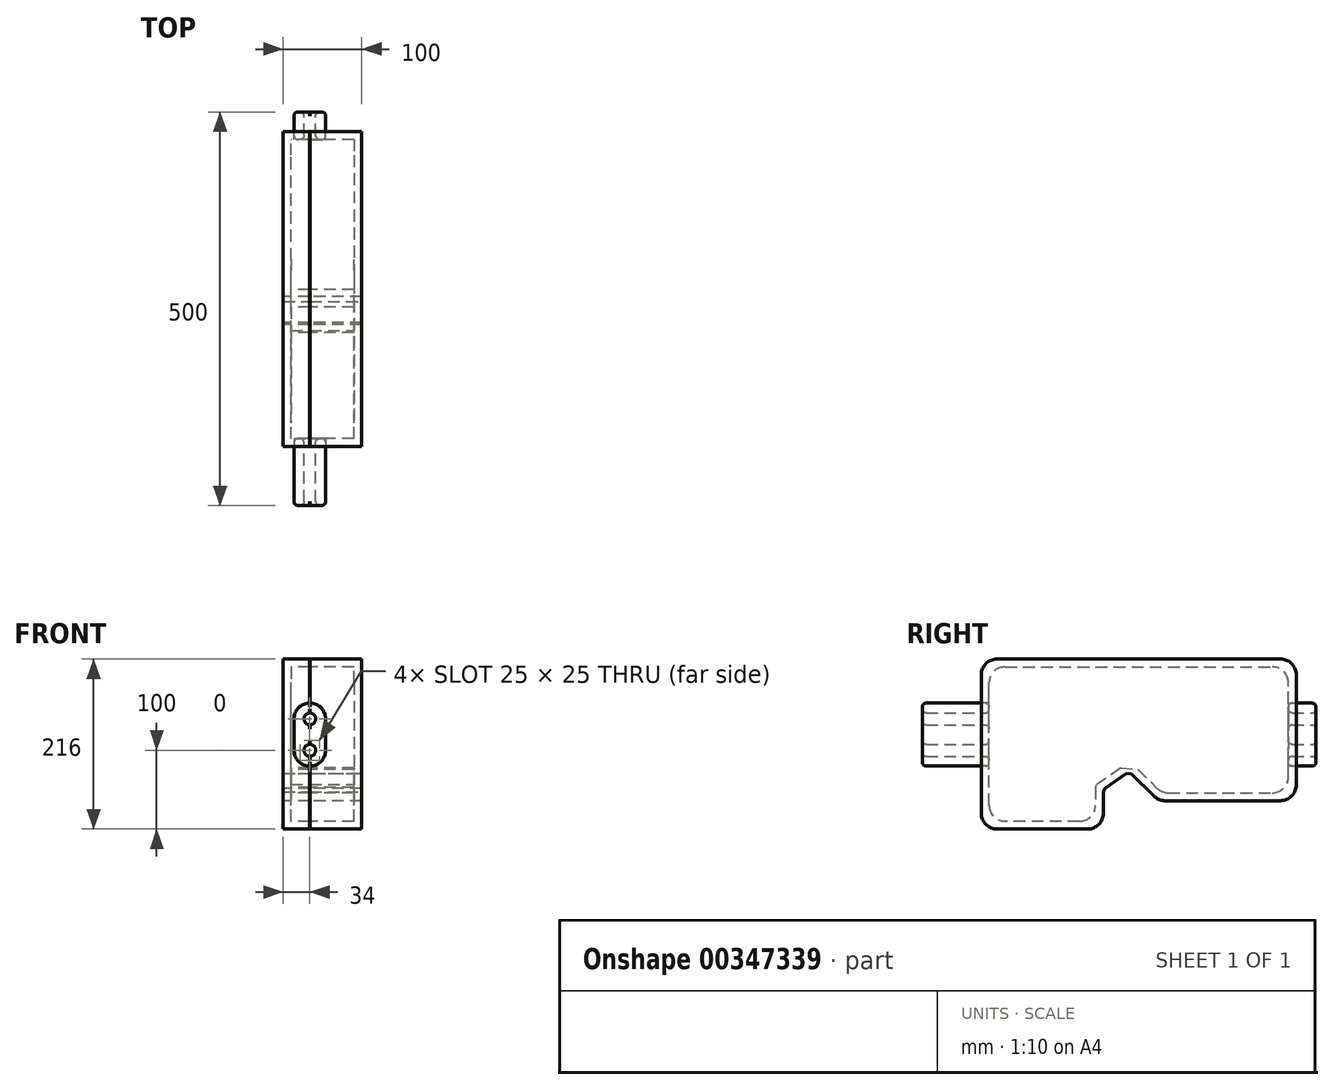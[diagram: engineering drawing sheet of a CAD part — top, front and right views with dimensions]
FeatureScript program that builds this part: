
annotation { "Feature Type Name" : "Feature", "Feature Type Description" : "" }
export const myFeature = defineFeature(function(context is Context, id is Id, definition is map)
    precondition{}
    {
        {
            var Q0;
            Q0=qCreatedBy(makeId("Right.planeOp"),FACE);
            var sketch = newSketch(context, id + "F0", { "sketchPlane" : qUnion([Q0])});
            skLineSegment(sketch, "E0.bottom", {"start": v(200, 75) * mm, "end": v(-200, 75) * mm});
            skLineSegment(sketch, "E0.left", {"start": v(200, 75) * mm, "end": v(200, -75) * mm});
            skLineSegment(sketch, "E0.right", {"start": v(-200, 75) * mm, "end": v(-200, -75) * mm});
            skPoint(sketch, "E0.middle", {"position": v(0, 0) * mm});
            skLineSegment(sketch, "E1", {"start": v(-200, -75) * mm, "end": v(-200, -141) * mm});
            skLineSegment(sketch, "E2", {"start": v(-200, -141) * mm, "end": v(-45, -141) * mm});
            skLineSegment(sketch, "E3", {"start": v(-45, -141) * mm, "end": v(-45, -91) * mm});
            skLineSegment(sketch, "E4", {"start": v(-12.23, -68.06) * mm, "end": v(-87.83, -68.06) * mm, "construction": true});
            skLineSegment(sketch, "E5", {"start": v(200, -75) * mm, "end": v(200, -105) * mm});
            skLineSegment(sketch, "E6", {"start": v(200, -105) * mm, "end": v(25, -105) * mm});
            skLineSegment(sketch, "E7", {"start": v(25, -105) * mm, "end": v(-12.23, -68.06) * mm});
            skLineSegment(sketch, "E8", {"start": v(-45, -91) * mm, "end": v(-12.23, -68.06) * mm});
            skSolve(sketch);
        }
        {
            var Q0;
            Q0=makeQuery(id+"F0.imprint","IMPRINT",FACE,{"disambiguationData":[TD([[makeQuery(id+"F0.imprint","IMPRINT",EDGE,{"derivedFrom":sQuery(id+"F0.wireOp",EDGE,"E0.bottom")}),1.0]])]});
            extrude(context, id + "F1", {"entities" : qUnion([Q0]), "depth" : 100 * mm});
        }
        {
            var Q0;
            Q0=makeQuery(id+"F1.opExtrude","CAP_FACE",FACE,{"disambiguationData":[OSD([sQuery(id+"F0.wireOp",EDGE,"E0.bottom"),sQuery(id+"F0.wireOp",EDGE,"E0.top"),sQuery(id+"F0.wireOp",EDGE,"E0.left"),sQuery(id+"F0.wireOp",EDGE,"E0.right")])],"isStart":true});
            shell(context, id + "F2", {"entities" : qUnion([Q0]), "thickness" : 10 * mm});
        }
        {
            var Q0;
            Q0=makeQuery(id+"F1.opExtrude","SWEPT_FACE",FACE,{"disambiguationData":[OSD([sQuery(id+"F0.wireOp",EDGE,"E0.left")])]});
            var sketch = newSketch(context, id + "F3", { "sketchPlane" : qUnion([Q0])});
            skCircle(sketch, "E9", {"center": v(-34, -41) * mm, "radius": 7.5 * mm});
            skCircle(sketch, "E10", {"center": v(-34, -1) * mm, "radius": 7.5 * mm});
            skLineSegment(sketch, "E11", {"start": v(-34, -1) * mm, "end": v(-34, -41) * mm, "construction": true});
            skLineSegment(sketch, "E12", {"start": v(-34, -1) * mm, "end": v(-100, -1) * mm, "construction": true});
            skLineSegment(sketch, "E13", {"start": v(-34, -1) * mm, "end": v(0, -1) * mm, "construction": true});
            skSolve(sketch);
        }
        {
            var Q0;
            Q0=qSketchRegion(id+"F3",true);
            extrude(context, id + "F4", {"entities" : qUnion([Q0]), "operationType" : NewBodyOperationType.REMOVE, "oppositeDirection" : true, "depth" : 1000 * mm});
        }
        {
            var Q0;
            Q0=makeQuery(id+"F1.opExtrude","CAP_FACE",FACE,{"disambiguationData":[OSD([sQuery(id+"F0.wireOp",EDGE,"E0.bottom"),sQuery(id+"F0.wireOp",EDGE,"E0.top"),sQuery(id+"F0.wireOp",EDGE,"E0.left"),sQuery(id+"F0.wireOp",EDGE,"E0.right")])],"isStart":true});
            var sketch = newSketch(context, id + "F5", { "sketchPlane" : qUnion([Q0])});
            skLineSegment(sketch, "E14", {"start": v(200, -141) * mm, "end": v(200, 75) * mm});
            skLineSegment(sketch, "E15", {"start": v(200, 75) * mm, "end": v(-200, 75) * mm});
            skLineSegment(sketch, "E16", {"start": v(-200, 75) * mm, "end": v(-200, 75) * mm});
            skLineSegment(sketch, "E17", {"start": v(45, -141) * mm, "end": v(45, -141) * mm});
            skLineSegment(sketch, "E18", {"start": v(45, -141) * mm, "end": v(200, -141) * mm});
            skLineSegment(sketch, "E19", {"start": v(-200, 75) * mm, "end": v(-200, -105) * mm});
            skLineSegment(sketch, "E20", {"start": v(-200, -105) * mm, "end": v(-200, -105) * mm});
            skLineSegment(sketch, "E21", {"start": v(-200, -105) * mm, "end": v(-25, -105) * mm});
            skLineSegment(sketch, "E22", {"start": v(-25, -105) * mm, "end": v(12.23, -68.06) * mm});
            skLineSegment(sketch, "E23", {"start": v(12.23, -68.06) * mm, "end": v(45, -91) * mm});
            skLineSegment(sketch, "E24", {"start": v(45, -91) * mm, "end": v(45, -141) * mm});
            skSolve(sketch);
        }
        {
            var Q0;
            Q0=qSketchRegion(id+"F5",true);
            extrude(context, id + "F6", {"entities" : qUnion([Q0]), "operationType" : NewBodyOperationType.ADD, "oppositeDirection" : true, "depth" : 10 * mm});
        }
        {
            var Q0;
            Q0=makeQuery(id+"F1.opExtrude","SWEPT_FACE",FACE,{"disambiguationData":[OSD([sQuery(id+"F0.wireOp",EDGE,"E2")])]});
            var sketch = newSketch(context, id + "F7", { "sketchPlane" : qUnion([Q0])});
            skLineSegment(sketch, "E25.bottom", {"start": v(33.95, 216.16) * mm, "end": v(34.05, 216.16) * mm});
            skLineSegment(sketch, "E25.top", {"start": v(33.95, -216.16) * mm, "end": v(34.05, -216.16) * mm});
            skLineSegment(sketch, "E25.left", {"start": v(33.95, 216.16) * mm, "end": v(33.95, -216.16) * mm});
            skLineSegment(sketch, "E25.right", {"start": v(34.05, 216.16) * mm, "end": v(34.05, -216.16) * mm});
            skPoint(sketch, "E25.middle", {"position": v(34, 0) * mm});
            skSolve(sketch);
        }
        {
            var Q0;
            Q0=qSketchRegion(id+"F7",true);
            extrude(context, id + "F8", {"entities" : qUnion([Q0]), "operationType" : NewBodyOperationType.REMOVE, "oppositeDirection" : true, "depth" : 583 * mm});
        }
        {
            var Q0;
            {var subQ0=sQuery(id+"F0.wireOp",EDGE,"E5");var subQ1=sQuery(id+"F0.wireOp",EDGE,"E0.left");var subQ2=makeQuery(id+"F1.opExtrude","SWEPT_FACE",FACE,{"disambiguationData":[OSD([subQ1,subQ0])]});Q0=makeQuery(id+"F8.boolean.opBoolean","SPLIT",FACE,{"disambiguationData":[TD([makeQuery(id+"F8.opExtrude","SWEPT_FACE",FACE,{"disambiguationData":[OSD([sQuery(id+"F7.wireOp",EDGE,"E25.right")])]})])],"derivedFrom":subQ2});}
            var sketch = newSketch(context, id + "F9", { "sketchPlane" : qUnion([Q0])});
            skLineSegment(sketch, "E26", {"start": v(-34, -1) * mm, "end": v(-34, -41) * mm, "construction": true});
            skLineSegment(sketch, "E27", {"start": v(-34, -1) * mm, "end": v(-14, -1) * mm, "construction": true});
            skLineSegment(sketch, "E28", {"start": v(-34, -1) * mm, "end": v(-54, -1) * mm, "construction": true});
            skArc(sketch, "E29", {"start": v(-14, -1) * mm, "mid": v(-34, 19) * mm, "end": v(-54, -1) * mm});
            skArc(sketch, "E30", {"start": v(-54, -41) * mm, "mid": v(-34, -61) * mm, "end": v(-14, -41) * mm});
            skPoint(sketch, "E30.endSnap0", {"position": v(-26.5, -41) * mm});
            skLineSegment(sketch, "E31", {"start": v(-14, -1) * mm, "end": v(-14, -41) * mm});
            skLineSegment(sketch, "E32", {"start": v(-54, -1) * mm, "end": v(-54, -41) * mm});
            skArc(sketch, "E33.0", {"start": v(-13.9, -1) * mm, "mid": v(-34, 19.1) * mm, "end": v(-54.1, -1) * mm});
            skLineSegment(sketch, "E33.1", {"start": v(-13.9, -1) * mm, "end": v(-13.9, -41) * mm});
            skArc(sketch, "E33.2", {"start": v(-54.1, -41) * mm, "mid": v(-34, -61.1) * mm, "end": v(-13.9, -41) * mm});
            skLineSegment(sketch, "E33.3", {"start": v(-54.1, -1) * mm, "end": v(-54.1, -41) * mm});
            skSolve(sketch);
        }
        {
            var Q0;
            Q0 = qSketchRegion(id + "F9", true);
            extrude(context, id + "F10", {"entities" : qUnion([Q0]), "operationType" : NewBodyOperationType.REMOVE, "oppositeDirection" : true, "depth" : 25 * mm});
        }
        {
            var Q0;
            {var subQ1=sQuery(id+"F0.wireOp",EDGE,"E1");var subQ2=sQuery(id+"F0.wireOp",EDGE,"E0.right");var subQ4=makeQuery(id+"F1.opExtrude","SWEPT_FACE",FACE,{"disambiguationData":[OSD([subQ2,subQ1])]});Q0=makeQuery(id+"F8.boolean.opBoolean","SPLIT",FACE,{"disambiguationData":[TD([makeQuery(id+"F8.opExtrude","SWEPT_FACE",FACE,{"disambiguationData":[OSD([sQuery(id+"F7.wireOp",EDGE,"E25.right")])]})])],"derivedFrom":subQ4});}
            var sketch = newSketch(context, id + "F11", { "sketchPlane" : qUnion([Q0])});
            skLineSegment(sketch, "E34", {"start": v(34, -41) * mm, "end": v(34, -1) * mm, "construction": true});
            skLineSegment(sketch, "E35", {"start": v(34, -1) * mm, "end": v(34, -41) * mm, "construction": true});
            skLineSegment(sketch, "E36", {"start": v(34, -1) * mm, "end": v(54, -1) * mm, "construction": true});
            skLineSegment(sketch, "E37", {"start": v(34, -1) * mm, "end": v(14, -1) * mm, "construction": true});
            skArc(sketch, "E38", {"start": v(54, -1) * mm, "mid": v(34, 19) * mm, "end": v(14, -1) * mm});
            skArc(sketch, "E39", {"start": v(14, -41) * mm, "mid": v(34, -61) * mm, "end": v(54, -41) * mm});
            skPoint(sketch, "E39.endSnap0", {"position": v(41.5, -41) * mm});
            skLineSegment(sketch, "E40", {"start": v(54, -1) * mm, "end": v(54, -41) * mm});
            skLineSegment(sketch, "E41", {"start": v(14, -1) * mm, "end": v(14, -41) * mm});
            skArc(sketch, "E42.0", {"start": v(54.1, -1) * mm, "mid": v(34, 19.1) * mm, "end": v(13.9, -1) * mm});
            skLineSegment(sketch, "E42.1", {"start": v(54.1, -1) * mm, "end": v(54.1, -41) * mm});
            skArc(sketch, "E42.2", {"start": v(13.9, -41) * mm, "mid": v(34, -61.1) * mm, "end": v(54.1, -41) * mm});
            skLineSegment(sketch, "E42.3", {"start": v(13.9, -1) * mm, "end": v(13.9, -41) * mm});
            skSolve(sketch);
        }
        {
            var Q0;
            Q0 = qSketchRegion(id + "F11", true);
            extrude(context, id + "F12", {"entities" : qUnion([Q0]), "operationType" : NewBodyOperationType.REMOVE, "oppositeDirection" : true, "depth" : 25 * mm});
        }
        {
            var Q0;
            {var subQ0=sQuery(id+"F0.wireOp",EDGE,"E5");var subQ1=sQuery(id+"F0.wireOp",EDGE,"E0.left");var subQ2=makeQuery(id+"F1.opExtrude","SWEPT_FACE",FACE,{"disambiguationData":[OSD([subQ1,subQ0])]});var subQ3=makeQuery(id+"F2.opShell","OFFSET_FACE",FACE,{"disambiguationData":[OSD([subQ1,subQ0])]});var subQ4=makeQuery(id+"F4.opExtrude","SWEPT_FACE",FACE,{"disambiguationData":[OSD([sQuery(id+"F3.wireOp",EDGE,"E10")])]});var subQ5=makeQuery(id+"F4.boolean.opBoolean","COPY",FACE,{"disambiguationData":[TD([subQ2])],"derivedFrom":subQ4});var subQ6=sQuery(id+"F0.wireOp",EDGE,"E0.bottom");var subQ7=sQuery(id+"F0.wireOp",EDGE,"E1");var subQ8=sQuery(id+"F0.wireOp",EDGE,"E0.right");var subQ9=makeQuery(id+"F1.opExtrude","SWEPT_FACE",FACE,{"disambiguationData":[OSD([subQ8,subQ7])]});var subQ10=makeQuery(id+"F2.opShell","OFFSET_FACE",FACE,{"disambiguationData":[OSD([subQ8,subQ7])]});Q0=makeQuery(id+"F10.boolean.opBoolean","SPLIT",FACE,{"disambiguationData":[TD([makeQuery(id+"F10.opExtrude","SWEPT_FACE",FACE,{"disambiguationData":[OSD([sQuery(id+"F9.wireOp",EDGE,"E29")])]})])],"derivedFrom":makeQuery(id+"F8.boolean.opBoolean","COPY",FACE,{"disambiguationData":[TD([makeQuery(id+"F1.opExtrude","SWEPT_FACE",FACE,{"disambiguationData":[OSD([subQ6])]}),subQ2,subQ9,makeQuery(id+"F2.opShell","OFFSET_FACE",FACE,{"disambiguationData":[OSD([subQ6])]}),subQ3,subQ10,subQ5,makeQuery(id+"F4.boolean.opBoolean","COPY",FACE,{"disambiguationData":[TD([subQ9])],"derivedFrom":subQ4})])],"derivedFrom":makeQuery(id+"F8.opExtrude","SWEPT_FACE",FACE,{"disambiguationData":[OSD([sQuery(id+"F7.wireOp",EDGE,"E25.right")])]})})});}
            var Q1;
            {var subQ0=sQuery(id+"F0.wireOp",EDGE,"E5");var subQ1=sQuery(id+"F0.wireOp",EDGE,"E0.left");var subQ2=makeQuery(id+"F1.opExtrude","SWEPT_FACE",FACE,{"disambiguationData":[OSD([subQ1,subQ0])]});var subQ3=makeQuery(id+"F2.opShell","OFFSET_FACE",FACE,{"disambiguationData":[OSD([subQ1,subQ0])]});Q1=makeQuery(id+"F8.boolean.opBoolean","COPY",FACE,{"disambiguationData":[TD([subQ2,subQ3,makeQuery(id+"F4.boolean.opBoolean","COPY",FACE,{"disambiguationData":[TD([subQ2])],"derivedFrom":makeQuery(id+"F4.opExtrude","SWEPT_FACE",FACE,{"disambiguationData":[OSD([sQuery(id+"F3.wireOp",EDGE,"E9")])]})}),makeQuery(id+"F4.boolean.opBoolean","COPY",FACE,{"disambiguationData":[TD([subQ2])],"derivedFrom":makeQuery(id+"F4.opExtrude","SWEPT_FACE",FACE,{"disambiguationData":[OSD([sQuery(id+"F3.wireOp",EDGE,"E10")])]})})])],"derivedFrom":makeQuery(id+"F8.opExtrude","SWEPT_FACE",FACE,{"disambiguationData":[OSD([sQuery(id+"F7.wireOp",EDGE,"E25.right")])]})});}
            var Q2;
            {var subQ0=sQuery(id+"F0.wireOp",EDGE,"E5");var subQ1=sQuery(id+"F0.wireOp",EDGE,"E0.left");var subQ2=makeQuery(id+"F1.opExtrude","SWEPT_FACE",FACE,{"disambiguationData":[OSD([subQ1,subQ0])]});var subQ3=makeQuery(id+"F2.opShell","OFFSET_FACE",FACE,{"disambiguationData":[OSD([subQ1,subQ0])]});var subQ4=makeQuery(id+"F4.opExtrude","SWEPT_FACE",FACE,{"disambiguationData":[OSD([sQuery(id+"F3.wireOp",EDGE,"E9")])]});var subQ5=makeQuery(id+"F4.boolean.opBoolean","COPY",FACE,{"disambiguationData":[TD([subQ2])],"derivedFrom":subQ4});var subQ6=sQuery(id+"F0.wireOp",EDGE,"548lelhJ-FumK-1v7O-jp4s-T3LJ27CFtbea");var subQ7=sQuery(id+"F0.wireOp",EDGE,"E2");var subQ8=sQuery(id+"F0.wireOp",EDGE,"BKIsQGDg-fWEg-7aJj-qOrJ-T1CRB7Qqrcyv");var subQ9=sQuery(id+"F0.wireOp",EDGE,"E1");var subQ10=sQuery(id+"F0.wireOp",EDGE,"E0.right");var subQ11=makeQuery(id+"F2.opShell","OFFSET_FACE",FACE,{"disambiguationData":[OSD([subQ10,subQ9])]});var subQ12=sQuery(id+"F0.wireOp",EDGE,"E6");var subQ13=makeQuery(id+"F1.opExtrude","SWEPT_FACE",FACE,{"disambiguationData":[OSD([subQ10,subQ9])]});var subQ14=sQuery(id+"F0.wireOp",EDGE,"E3");Q2=makeQuery(id+"F10.boolean.opBoolean","SPLIT",FACE,{"disambiguationData":[TD([makeQuery(id+"F10.opExtrude","SWEPT_FACE",FACE,{"disambiguationData":[OSD([sQuery(id+"F9.wireOp",EDGE,"E30")])]})])],"derivedFrom":makeQuery(id+"F8.boolean.opBoolean","COPY",FACE,{"disambiguationData":[TD([subQ2,subQ13,makeQuery(id+"F1.opExtrude","SWEPT_FACE",FACE,{"disambiguationData":[OSD([subQ7])]}),makeQuery(id+"F1.opExtrude","SWEPT_FACE",FACE,{"disambiguationData":[OSD([subQ14])]}),makeQuery(id+"F1.opExtrude","SWEPT_FACE",FACE,{"disambiguationData":[OSD([subQ12])]}),makeQuery(id+"F1.opExtrude","SWEPT_FACE",FACE,{"disambiguationData":[OSD([subQ8])]}),makeQuery(id+"F1.opExtrude","SWEPT_FACE",FACE,{"disambiguationData":[OSD([subQ6])]}),subQ3,subQ11,makeQuery(id+"F2.opShell","OFFSET_FACE",FACE,{"disambiguationData":[OSD([subQ7])]}),makeQuery(id+"F2.opShell","OFFSET_FACE",FACE,{"disambiguationData":[OSD([subQ14])]}),makeQuery(id+"F2.opShell","OFFSET_FACE",FACE,{"disambiguationData":[OSD([subQ12])]}),makeQuery(id+"F2.opShell","OFFSET_FACE",FACE,{"disambiguationData":[OSD([subQ8])]}),makeQuery(id+"F2.opShell","OFFSET_FACE",FACE,{"disambiguationData":[OSD([subQ6])]}),subQ5,makeQuery(id+"F4.boolean.opBoolean","COPY",FACE,{"disambiguationData":[TD([subQ13])],"derivedFrom":subQ4})])],"derivedFrom":makeQuery(id+"F8.opExtrude","SWEPT_FACE",FACE,{"disambiguationData":[OSD([sQuery(id+"F7.wireOp",EDGE,"E25.right")])]})})});}
            extrude(context, id + "F13", {"entities" : qUnion([Q0, Q1, Q2]), "operationType" : NewBodyOperationType.ADD, "depth" : 0.1 * mm});
        }
        {
            var Q0;
            {var subQ0=sQuery(id+"F0.wireOp",EDGE,"E1");var subQ1=sQuery(id+"F0.wireOp",EDGE,"E0.right");var subQ2=makeQuery(id+"F1.opExtrude","SWEPT_FACE",FACE,{"disambiguationData":[OSD([subQ1,subQ0])]});var subQ3=makeQuery(id+"F2.opShell","OFFSET_FACE",FACE,{"disambiguationData":[OSD([subQ1,subQ0])]});var subQ4=makeQuery(id+"F4.opExtrude","SWEPT_FACE",FACE,{"disambiguationData":[OSD([sQuery(id+"F3.wireOp",EDGE,"E9")])]});var subQ5=makeQuery(id+"F4.boolean.opBoolean","COPY",FACE,{"disambiguationData":[TD([subQ2])],"derivedFrom":subQ4});var subQ6=sQuery(id+"F0.wireOp",EDGE,"548lelhJ-FumK-1v7O-jp4s-T3LJ27CFtbea");var subQ7=makeQuery(id+"F1.opExtrude","SWEPT_FACE",FACE,{"disambiguationData":[OSD([subQ6])]});var subQ8=sQuery(id+"F0.wireOp",EDGE,"E2");var subQ9=makeQuery(id+"F2.opShell","OFFSET_FACE",FACE,{"disambiguationData":[OSD([subQ8])]});var subQ18=makeQuery(id+"F1.opExtrude","SWEPT_FACE",FACE,{"disambiguationData":[OSD([subQ8])]});var subQ19=sQuery(id+"F0.wireOp",EDGE,"E3");var subQ20=makeQuery(id+"F1.opExtrude","SWEPT_FACE",FACE,{"disambiguationData":[OSD([subQ19])]});var subQ21=sQuery(id+"F0.wireOp",EDGE,"BKIsQGDg-fWEg-7aJj-qOrJ-T1CRB7Qqrcyv");var subQ22=sQuery(id+"F0.wireOp",EDGE,"E6");var subQ23=sQuery(id+"F0.wireOp",EDGE,"E5");var subQ24=sQuery(id+"F0.wireOp",EDGE,"E0.left");var subQ26=makeQuery(id+"F8.opExtrude","SWEPT_FACE",FACE,{"disambiguationData":[OSD([sQuery(id+"F7.wireOp",EDGE,"E25.left")])]});var subQ27=makeQuery(id+"F1.opExtrude","SWEPT_FACE",FACE,{"disambiguationData":[OSD([subQ21])]});var subQ29=makeQuery(id+"F1.opExtrude","SWEPT_FACE",FACE,{"disambiguationData":[OSD([subQ22])]});var subQ30=makeQuery(id+"F1.opExtrude","SWEPT_FACE",FACE,{"disambiguationData":[OSD([subQ24,subQ23])]});var subQ31=makeQuery(id+"F2.opShell","OFFSET_FACE",FACE,{"disambiguationData":[OSD([subQ24,subQ23])]});var subQ32=makeQuery(id+"F2.opShell","OFFSET_FACE",FACE,{"disambiguationData":[OSD([subQ19])]});var subQ33=makeQuery(id+"F2.opShell","OFFSET_FACE",FACE,{"disambiguationData":[OSD([subQ22])]});var subQ34=makeQuery(id+"F2.opShell","OFFSET_FACE",FACE,{"disambiguationData":[OSD([subQ21])]});var subQ35=makeQuery(id+"F2.opShell","OFFSET_FACE",FACE,{"disambiguationData":[OSD([subQ6])]});Q0=makeQuery(id+"F12.boolean.opBoolean","SPLIT",FACE,{"disambiguationData":[TD([makeQuery(id+"F12.opExtrude","SWEPT_FACE",FACE,{"disambiguationData":[OSD([sQuery(id+"F11.wireOp",EDGE,"E39")])]})])],"derivedFrom":makeQuery(id+"F10.boolean.opBoolean","SPLIT",FACE,{"disambiguationData":[TD([subQ18])],"derivedFrom":makeQuery(id+"F8.boolean.opBoolean","COPY",FACE,{"disambiguationData":[TD([subQ30,subQ2,subQ18,subQ20,subQ29,subQ27,subQ7,subQ31,subQ3,subQ9,subQ32,subQ33,subQ34,subQ35,makeQuery(id+"F4.boolean.opBoolean","COPY",FACE,{"disambiguationData":[TD([subQ30])],"derivedFrom":subQ4}),subQ5])],"derivedFrom":subQ26})})});}
            var Q1;
            {var subQ0=sQuery(id+"F0.wireOp",EDGE,"E1");var subQ1=sQuery(id+"F0.wireOp",EDGE,"E0.right");var subQ2=makeQuery(id+"F1.opExtrude","SWEPT_FACE",FACE,{"disambiguationData":[OSD([subQ1,subQ0])]});var subQ3=makeQuery(id+"F2.opShell","OFFSET_FACE",FACE,{"disambiguationData":[OSD([subQ1,subQ0])]});Q1=makeQuery(id+"F8.boolean.opBoolean","COPY",FACE,{"disambiguationData":[TD([subQ2,subQ3,makeQuery(id+"F4.boolean.opBoolean","COPY",FACE,{"disambiguationData":[TD([subQ2])],"derivedFrom":makeQuery(id+"F4.opExtrude","SWEPT_FACE",FACE,{"disambiguationData":[OSD([sQuery(id+"F3.wireOp",EDGE,"E9")])]})}),makeQuery(id+"F4.boolean.opBoolean","COPY",FACE,{"disambiguationData":[TD([subQ2])],"derivedFrom":makeQuery(id+"F4.opExtrude","SWEPT_FACE",FACE,{"disambiguationData":[OSD([sQuery(id+"F3.wireOp",EDGE,"E10")])]})})])],"derivedFrom":makeQuery(id+"F8.opExtrude","SWEPT_FACE",FACE,{"disambiguationData":[OSD([sQuery(id+"F7.wireOp",EDGE,"E25.left")])]})});}
            var Q2;
            {var subQ0=sQuery(id+"F0.wireOp",EDGE,"E1");var subQ1=sQuery(id+"F0.wireOp",EDGE,"E0.right");var subQ2=makeQuery(id+"F1.opExtrude","SWEPT_FACE",FACE,{"disambiguationData":[OSD([subQ1,subQ0])]});var subQ3=makeQuery(id+"F2.opShell","OFFSET_FACE",FACE,{"disambiguationData":[OSD([subQ1,subQ0])]});var subQ4=makeQuery(id+"F4.opExtrude","SWEPT_FACE",FACE,{"disambiguationData":[OSD([sQuery(id+"F3.wireOp",EDGE,"E10")])]});var subQ5=makeQuery(id+"F4.boolean.opBoolean","COPY",FACE,{"disambiguationData":[TD([subQ2])],"derivedFrom":subQ4});var subQ6=sQuery(id+"F0.wireOp",EDGE,"E0.bottom");var subQ7=makeQuery(id+"F2.opShell","OFFSET_FACE",FACE,{"disambiguationData":[OSD([subQ6])]});var subQ8=sQuery(id+"F0.wireOp",EDGE,"E5");var subQ9=sQuery(id+"F0.wireOp",EDGE,"E0.left");var subQ10=makeQuery(id+"F1.opExtrude","SWEPT_FACE",FACE,{"disambiguationData":[OSD([subQ9,subQ8])]});var subQ11=makeQuery(id+"F1.opExtrude","SWEPT_FACE",FACE,{"disambiguationData":[OSD([subQ6])]});var subQ12=makeQuery(id+"F2.opShell","OFFSET_FACE",FACE,{"disambiguationData":[OSD([subQ9,subQ8])]});Q2=makeQuery(id+"F12.boolean.opBoolean","SPLIT",FACE,{"disambiguationData":[TD([makeQuery(id+"F12.opExtrude","SWEPT_FACE",FACE,{"disambiguationData":[OSD([sQuery(id+"F11.wireOp",EDGE,"E38")])]})])],"derivedFrom":makeQuery(id+"F10.boolean.opBoolean","SPLIT",FACE,{"disambiguationData":[TD([subQ11])],"derivedFrom":makeQuery(id+"F8.boolean.opBoolean","COPY",FACE,{"disambiguationData":[TD([subQ11,subQ10,subQ2,subQ7,subQ12,subQ3,makeQuery(id+"F4.boolean.opBoolean","COPY",FACE,{"disambiguationData":[TD([subQ10])],"derivedFrom":subQ4}),subQ5])],"derivedFrom":makeQuery(id+"F8.opExtrude","SWEPT_FACE",FACE,{"disambiguationData":[OSD([sQuery(id+"F7.wireOp",EDGE,"E25.left")])]})})})});}
            extrude(context, id + "F14", {"entities" : qUnion([Q0, Q1, Q2]), "operationType" : NewBodyOperationType.ADD, "depth" : 0.1 * mm});
        }
        {
            var Q0;
            {var subQ0=sQuery(id+"F0.wireOp",EDGE,"E8");var subQ1=sQuery(id+"F0.wireOp",EDGE,"E7");Q0=makeQuery(id+"F8.boolean.opBoolean","SPLIT",EDGE,{"disambiguationData":[TD([makeQuery(id+"F8.opExtrude","SWEPT_FACE",FACE,{"disambiguationData":[OSD([sQuery(id+"F7.wireOp",EDGE,"E25.right")])]})])],"derivedFrom":makeQuery(id+"F1.opExtrude","SWEPT_EDGE",EDGE,{"disambiguationData":[OSD([subQ1,subQ0])]})});}
            var Q1;
            {var subQ0=sQuery(id+"F0.wireOp",EDGE,"E8");var subQ1=sQuery(id+"F0.wireOp",EDGE,"E7");Q1=makeQuery(id+"F8.boolean.opBoolean","SPLIT",EDGE,{"disambiguationData":[TD([makeQuery(id+"F8.opExtrude","SWEPT_FACE",FACE,{"disambiguationData":[OSD([sQuery(id+"F7.wireOp",EDGE,"E25.left")])]})])],"derivedFrom":makeQuery(id+"F1.opExtrude","SWEPT_EDGE",EDGE,{"disambiguationData":[OSD([subQ1,subQ0])]})});}
            var Q2;
            {var subQ0=sQuery(id+"F0.wireOp",EDGE,"E8");var subQ1=sQuery(id+"F0.wireOp",EDGE,"E3");Q2=makeQuery(id+"F8.boolean.opBoolean","SPLIT",EDGE,{"disambiguationData":[TD([makeQuery(id+"F8.opExtrude","SWEPT_FACE",FACE,{"disambiguationData":[OSD([sQuery(id+"F7.wireOp",EDGE,"E25.right")])]})])],"derivedFrom":makeQuery(id+"F1.opExtrude","SWEPT_EDGE",EDGE,{"disambiguationData":[OSD([subQ1,subQ0])]})});}
            var Q3;
            {var subQ0=sQuery(id+"F0.wireOp",EDGE,"E8");var subQ1=sQuery(id+"F0.wireOp",EDGE,"E3");Q3=makeQuery(id+"F8.boolean.opBoolean","SPLIT",EDGE,{"disambiguationData":[TD([makeQuery(id+"F8.opExtrude","SWEPT_FACE",FACE,{"disambiguationData":[OSD([sQuery(id+"F7.wireOp",EDGE,"E25.left")])]})])],"derivedFrom":makeQuery(id+"F1.opExtrude","SWEPT_EDGE",EDGE,{"disambiguationData":[OSD([subQ1,subQ0])]})});}
            var Q4;
            {var subQ0=sQuery(id+"F0.wireOp",EDGE,"E3");var subQ1=sQuery(id+"F0.wireOp",EDGE,"E8");Q4=makeQuery(id+"F8.boolean.opBoolean","SPLIT",EDGE,{"disambiguationData":[TD([makeQuery(id+"F8.opExtrude","SWEPT_FACE",FACE,{"disambiguationData":[OSD([sQuery(id+"F7.wireOp",EDGE,"E25.left")])]})])],"derivedFrom":makeQuery(id+"F2.opShell","OFFSET_EDGE",EDGE,{"disambiguationData":[OSD([subQ0,subQ1])]})});}
            var Q5;
            {var subQ0=sQuery(id+"F0.wireOp",EDGE,"E8");var subQ1=sQuery(id+"F0.wireOp",EDGE,"E3");Q5=makeQuery(id+"F8.boolean.opBoolean","SPLIT",EDGE,{"disambiguationData":[TD([makeQuery(id+"F8.opExtrude","SWEPT_FACE",FACE,{"disambiguationData":[OSD([sQuery(id+"F7.wireOp",EDGE,"E25.right")])]})])],"derivedFrom":makeQuery(id+"F2.opShell","OFFSET_EDGE",EDGE,{"disambiguationData":[OSD([subQ1,subQ0])]})});}
            var Q6;
            {var subQ0=sQuery(id+"F0.wireOp",EDGE,"E7");var subQ1=sQuery(id+"F0.wireOp",EDGE,"E8");Q6=makeQuery(id+"F8.boolean.opBoolean","SPLIT",EDGE,{"disambiguationData":[TD([makeQuery(id+"F8.opExtrude","SWEPT_FACE",FACE,{"disambiguationData":[OSD([sQuery(id+"F7.wireOp",EDGE,"E25.left")])]})])],"derivedFrom":makeQuery(id+"F2.opShell","OFFSET_EDGE",EDGE,{"disambiguationData":[OSD([subQ0,subQ1])]})});}
            var Q7;
            {var subQ0=sQuery(id+"F0.wireOp",EDGE,"E8");var subQ1=sQuery(id+"F0.wireOp",EDGE,"E7");Q7=makeQuery(id+"F8.boolean.opBoolean","SPLIT",EDGE,{"disambiguationData":[TD([makeQuery(id+"F8.opExtrude","SWEPT_FACE",FACE,{"disambiguationData":[OSD([sQuery(id+"F7.wireOp",EDGE,"E25.right")])]})])],"derivedFrom":makeQuery(id+"F2.opShell","OFFSET_EDGE",EDGE,{"disambiguationData":[OSD([subQ1,subQ0])]})});}
            chamfer(context, id + "F15", {"entities" : qUnion([Q0, Q1, Q2, Q3, Q4, Q5, Q6, Q7]), "width" : 5 * mm, "tangentPropagation" : true});
        }
        {
            var Q0;
            Q0=makeQuery(id+"F6.opExtrude","CAP_FACE",FACE,{"disambiguationData":[OSD([sQuery(id+"F5.wireOp",EDGE,"E14"),sQuery(id+"F5.wireOp",EDGE,"E15"),sQuery(id+"F5.wireOp",EDGE,"E18"),sQuery(id+"F5.wireOp",EDGE,"E19"),sQuery(id+"F5.wireOp",EDGE,"E21"),sQuery(id+"F5.wireOp",EDGE,"E22"),sQuery(id+"F5.wireOp",EDGE,"E23"),sQuery(id+"F5.wireOp",EDGE,"E24")])],"isStart":false});
            var sketch = newSketch(context, id + "F16", { "sketchPlane" : qUnion([Q0])});
            skLineSegment(sketch, "E43", {"start": v(-36.84, -62.15) * mm, "end": v(25.94, -67.52) * mm});
            skLineSegment(sketch, "E44", {"start": v(-36.84, -62.15) * mm, "end": v(-2.16, -41.68) * mm});
            skLineSegment(sketch, "E45", {"start": v(-2.16, -41.68) * mm, "end": v(25.94, -67.52) * mm});
            skSolve(sketch);
        }
        {
            var Q0;
            Q0 = qSketchRegion(id + "F16", true);
            extrude(context, id + "F17", {"entities" : qUnion([Q0]), "operationType" : NewBodyOperationType.REMOVE, "depth" : 80 * mm});
        }
        {
            var Q0;
            {var subQ0=sQuery(id+"F0.wireOp",EDGE,"E5");var subQ1=sQuery(id+"F0.wireOp",EDGE,"E0.left");var subQ2=makeQuery(id+"F1.opExtrude","SWEPT_FACE",FACE,{"disambiguationData":[OSD([subQ1,subQ0])]});var subQ26=sQuery(id+"F7.wireOp",EDGE,"E25.right");var subQ27=makeQuery(id+"F8.opExtrude","SWEPT_FACE",FACE,{"disambiguationData":[OSD([subQ26])]});var subQ29=makeQuery(id+"F10.opExtrude","SWEPT_FACE",FACE,{"disambiguationData":[OSD([sQuery(id+"F9.wireOp",EDGE,"E30")])]});var subQ30=subQ2;var subQ33=makeQuery(id+"F10.opExtrude","SWEPT_FACE",FACE,{"disambiguationData":[OSD([sQuery(id+"F9.wireOp",EDGE,"E29")])]});var subQ39=makeQuery(id+"F8.opExtrude","SWEPT_FACE",FACE,{"disambiguationData":[OSD([sQuery(id+"F7.wireOp",EDGE,"E25.left")])]});Q0=makeQuery(id+"F13.boolean.opBoolean","MERGE",FACE,{"derivedFrom":[makeQuery(id+"F10.boolean.opBoolean","SPLIT",FACE,{"disambiguationData":[TD([subQ33])],"derivedFrom":makeQuery(id+"F8.boolean.opBoolean","SPLIT",FACE,{"disambiguationData":[TD([subQ39])],"derivedFrom":subQ30})}),makeQuery(id+"F10.boolean.opBoolean","SPLIT",FACE,{"disambiguationData":[TD([subQ33])],"derivedFrom":makeQuery(id+"F8.boolean.opBoolean","SPLIT",FACE,{"disambiguationData":[TD([subQ27])],"derivedFrom":subQ30})}),makeQuery(id+"F13.opExtrude","SWEPT_FACE",FACE,{"disambiguationData":[OSD([subQ1,subQ0,subQ26]),TDD([makeQuery(id+"F8.boolean.opBoolean","INTERSECT",EDGE,{"disambiguationData":[OD(2.0)],"derivedFrom":[subQ30,subQ27]})])]}),makeQuery(id+"F13.opExtrude","SWEPT_FACE",FACE,{"disambiguationData":[OSD([subQ1,subQ0,subQ26]),TDD([makeQuery(id+"F10.boolean.opBoolean","SPLIT",EDGE,{"disambiguationData":[TD([subQ33])],"derivedFrom":makeQuery(id+"F8.boolean.opBoolean","INTERSECT",EDGE,{"disambiguationData":[OD(0.0)],"derivedFrom":[subQ30,subQ27]})})])]}),makeQuery(id+"F13.opExtrude","SWEPT_FACE",FACE,{"disambiguationData":[OSD([subQ1,subQ0,subQ26]),TDD([makeQuery(id+"F10.boolean.opBoolean","SPLIT",EDGE,{"disambiguationData":[TD([subQ29])],"derivedFrom":makeQuery(id+"F8.boolean.opBoolean","INTERSECT",EDGE,{"disambiguationData":[OD(1.0)],"derivedFrom":[subQ30,subQ27]})})])]})]});}
            extrude(context, id + "F18", {"entities" : qUnion([Q0]), "operationType" : NewBodyOperationType.ADD, "depth" : 25 * mm});
        }
        {
            var Q0;
            {var subQ0=sQuery(id+"F0.wireOp",EDGE,"E1");var subQ1=sQuery(id+"F0.wireOp",EDGE,"E0.right");var subQ2=makeQuery(id+"F1.opExtrude","SWEPT_FACE",FACE,{"disambiguationData":[OSD([subQ1,subQ0])]});var subQ26=sQuery(id+"F7.wireOp",EDGE,"E25.left");var subQ27=makeQuery(id+"F8.opExtrude","SWEPT_FACE",FACE,{"disambiguationData":[OSD([subQ26])]});var subQ29=makeQuery(id+"F12.opExtrude","SWEPT_FACE",FACE,{"disambiguationData":[OSD([sQuery(id+"F11.wireOp",EDGE,"E39")])]});var subQ30=subQ2;var subQ38=makeQuery(id+"F12.opExtrude","SWEPT_FACE",FACE,{"disambiguationData":[OSD([sQuery(id+"F11.wireOp",EDGE,"E38")])]});var subQ39=makeQuery(id+"F8.opExtrude","SWEPT_FACE",FACE,{"disambiguationData":[OSD([sQuery(id+"F7.wireOp",EDGE,"E25.right")])]});Q0=makeQuery(id+"F14.boolean.opBoolean","MERGE",FACE,{"derivedFrom":[makeQuery(id+"F12.boolean.opBoolean","SPLIT",FACE,{"disambiguationData":[TD([subQ38])],"derivedFrom":makeQuery(id+"F8.boolean.opBoolean","SPLIT",FACE,{"disambiguationData":[TD([subQ27])],"derivedFrom":subQ30})}),makeQuery(id+"F12.boolean.opBoolean","SPLIT",FACE,{"disambiguationData":[TD([subQ38])],"derivedFrom":makeQuery(id+"F8.boolean.opBoolean","SPLIT",FACE,{"disambiguationData":[TD([subQ39])],"derivedFrom":subQ30})}),makeQuery(id+"F14.opExtrude","SWEPT_FACE",FACE,{"disambiguationData":[OSD([subQ1,subQ0,subQ26]),TDD([makeQuery(id+"F8.boolean.opBoolean","INTERSECT",EDGE,{"disambiguationData":[OD(2.0)],"derivedFrom":[subQ30,subQ27]})])]}),makeQuery(id+"F14.opExtrude","SWEPT_FACE",FACE,{"disambiguationData":[OSD([subQ1,subQ0,subQ26]),TDD([makeQuery(id+"F12.boolean.opBoolean","SPLIT",EDGE,{"disambiguationData":[TD([subQ38])],"derivedFrom":makeQuery(id+"F8.boolean.opBoolean","INTERSECT",EDGE,{"disambiguationData":[OD(0.0)],"derivedFrom":[subQ30,subQ27]})})])]}),makeQuery(id+"F14.opExtrude","SWEPT_FACE",FACE,{"disambiguationData":[OSD([subQ1,subQ0,subQ26]),TDD([makeQuery(id+"F12.boolean.opBoolean","SPLIT",EDGE,{"disambiguationData":[TD([subQ29])],"derivedFrom":makeQuery(id+"F8.boolean.opBoolean","INTERSECT",EDGE,{"disambiguationData":[OD(1.0)],"derivedFrom":[subQ30,subQ27]})})])]})]});}
            extrude(context, id + "F19", {"entities" : qUnion([Q0]), "operationType" : NewBodyOperationType.ADD, "depth" : 75 * mm});
        }
        {
            var Q0;
            {var subQ0=sQuery(id+"F0.wireOp",EDGE,"E0.bottom");var subQ2=sQuery(id+"F0.wireOp",EDGE,"E0.right");Q0=makeQuery(id+"F8.boolean.opBoolean","SPLIT",EDGE,{"disambiguationData":[TD([makeQuery(id+"F8.opExtrude","SWEPT_FACE",FACE,{"disambiguationData":[OSD([sQuery(id+"F7.wireOp",EDGE,"E25.left")])]})])],"derivedFrom":makeQuery(id+"F1.opExtrude","SWEPT_EDGE",EDGE,{"disambiguationData":[OSD([subQ0,subQ2])]})});}
            var Q1;
            {var subQ0=sQuery(id+"F0.wireOp",EDGE,"E0.bottom");var subQ2=sQuery(id+"F0.wireOp",EDGE,"E0.right");Q1=makeQuery(id+"F8.boolean.opBoolean","SPLIT",EDGE,{"disambiguationData":[TD([makeQuery(id+"F8.opExtrude","SWEPT_FACE",FACE,{"disambiguationData":[OSD([sQuery(id+"F7.wireOp",EDGE,"E25.right")])]})])],"derivedFrom":makeQuery(id+"F1.opExtrude","SWEPT_EDGE",EDGE,{"disambiguationData":[OSD([subQ0,subQ2])]})});}
            var Q2;
            {var subQ0=sQuery(id+"F0.wireOp",EDGE,"E0.bottom");var subQ1=sQuery(id+"F0.wireOp",EDGE,"E0.right");Q2=makeQuery(id+"F8.boolean.opBoolean","SPLIT",EDGE,{"disambiguationData":[TD([makeQuery(id+"F8.opExtrude","SWEPT_FACE",FACE,{"disambiguationData":[OSD([sQuery(id+"F7.wireOp",EDGE,"E25.left")])]})])],"derivedFrom":makeQuery(id+"F2.opShell","OFFSET_EDGE",EDGE,{"disambiguationData":[OSD([subQ0,subQ1])]})});}
            var Q3;
            {var subQ0=sQuery(id+"F0.wireOp",EDGE,"E0.bottom");var subQ2=sQuery(id+"F0.wireOp",EDGE,"E0.right");Q3=makeQuery(id+"F8.boolean.opBoolean","SPLIT",EDGE,{"disambiguationData":[TD([makeQuery(id+"F8.opExtrude","SWEPT_FACE",FACE,{"disambiguationData":[OSD([sQuery(id+"F7.wireOp",EDGE,"E25.right")])]})])],"derivedFrom":makeQuery(id+"F2.opShell","OFFSET_EDGE",EDGE,{"disambiguationData":[OSD([subQ0,subQ2])]})});}
            var Q4;
            {var subQ0=sQuery(id+"F0.wireOp",EDGE,"E2");var subQ1=sQuery(id+"F0.wireOp",EDGE,"E1");Q4=makeQuery(id+"F8.boolean.opBoolean","SPLIT",EDGE,{"disambiguationData":[TD([makeQuery(id+"F8.opExtrude","SWEPT_FACE",FACE,{"disambiguationData":[OSD([sQuery(id+"F7.wireOp",EDGE,"E25.left")])]})])],"derivedFrom":makeQuery(id+"F1.opExtrude","SWEPT_EDGE",EDGE,{"disambiguationData":[OSD([subQ1,subQ0])]})});}
            var Q5;
            {var subQ0=sQuery(id+"F0.wireOp",EDGE,"E2");var subQ1=sQuery(id+"F0.wireOp",EDGE,"E1");Q5=makeQuery(id+"F8.boolean.opBoolean","SPLIT",EDGE,{"disambiguationData":[TD([makeQuery(id+"F8.opExtrude","SWEPT_FACE",FACE,{"disambiguationData":[OSD([sQuery(id+"F7.wireOp",EDGE,"E25.right")])]})])],"derivedFrom":makeQuery(id+"F1.opExtrude","SWEPT_EDGE",EDGE,{"disambiguationData":[OSD([subQ1,subQ0])]})});}
            var Q6;
            {var subQ0=sQuery(id+"F0.wireOp",EDGE,"E2");var subQ1=sQuery(id+"F0.wireOp",EDGE,"E1");Q6=makeQuery(id+"F8.boolean.opBoolean","SPLIT",EDGE,{"disambiguationData":[TD([makeQuery(id+"F8.opExtrude","SWEPT_FACE",FACE,{"disambiguationData":[OSD([sQuery(id+"F7.wireOp",EDGE,"E25.right")])]})])],"derivedFrom":makeQuery(id+"F2.opShell","OFFSET_EDGE",EDGE,{"disambiguationData":[OSD([subQ1,subQ0])]})});}
            var Q7;
            {var subQ0=sQuery(id+"F0.wireOp",EDGE,"E1");var subQ1=sQuery(id+"F0.wireOp",EDGE,"E2");Q7=makeQuery(id+"F8.boolean.opBoolean","SPLIT",EDGE,{"disambiguationData":[TD([makeQuery(id+"F8.opExtrude","SWEPT_FACE",FACE,{"disambiguationData":[OSD([sQuery(id+"F7.wireOp",EDGE,"E25.left")])]})])],"derivedFrom":makeQuery(id+"F2.opShell","OFFSET_EDGE",EDGE,{"disambiguationData":[OSD([subQ0,subQ1])]})});}
            var Q8;
            {var subQ0=sQuery(id+"F0.wireOp",EDGE,"E3");var subQ1=sQuery(id+"F0.wireOp",EDGE,"E2");Q8=makeQuery(id+"F8.boolean.opBoolean","SPLIT",EDGE,{"disambiguationData":[TD([makeQuery(id+"F8.opExtrude","SWEPT_FACE",FACE,{"disambiguationData":[OSD([sQuery(id+"F7.wireOp",EDGE,"E25.right")])]})])],"derivedFrom":makeQuery(id+"F1.opExtrude","SWEPT_EDGE",EDGE,{"disambiguationData":[OSD([subQ1,subQ0])]})});}
            var Q9;
            {var subQ0=sQuery(id+"F0.wireOp",EDGE,"E2");var subQ1=sQuery(id+"F0.wireOp",EDGE,"E3");Q9=makeQuery(id+"F8.boolean.opBoolean","SPLIT",EDGE,{"disambiguationData":[TD([makeQuery(id+"F8.opExtrude","SWEPT_FACE",FACE,{"disambiguationData":[OSD([sQuery(id+"F7.wireOp",EDGE,"E25.left")])]})])],"derivedFrom":makeQuery(id+"F1.opExtrude","SWEPT_EDGE",EDGE,{"disambiguationData":[OSD([subQ0,subQ1])]})});}
            var Q10;
            {var subQ0=sQuery(id+"F0.wireOp",EDGE,"E2");var subQ1=sQuery(id+"F0.wireOp",EDGE,"E3");Q10=makeQuery(id+"F8.boolean.opBoolean","SPLIT",EDGE,{"disambiguationData":[TD([makeQuery(id+"F8.opExtrude","SWEPT_FACE",FACE,{"disambiguationData":[OSD([sQuery(id+"F7.wireOp",EDGE,"E25.left")])]})])],"derivedFrom":makeQuery(id+"F2.opShell","OFFSET_EDGE",EDGE,{"disambiguationData":[OSD([subQ0,subQ1])]})});}
            var Q11;
            {var subQ0=sQuery(id+"F0.wireOp",EDGE,"E3");var subQ1=sQuery(id+"F0.wireOp",EDGE,"E2");Q11=makeQuery(id+"F8.boolean.opBoolean","SPLIT",EDGE,{"disambiguationData":[TD([makeQuery(id+"F8.opExtrude","SWEPT_FACE",FACE,{"disambiguationData":[OSD([sQuery(id+"F7.wireOp",EDGE,"E25.right")])]})])],"derivedFrom":makeQuery(id+"F2.opShell","OFFSET_EDGE",EDGE,{"disambiguationData":[OSD([subQ1,subQ0])]})});}
            var Q12;
            {var subQ0=sQuery(id+"F0.wireOp",EDGE,"E7");var subQ1=sQuery(id+"F0.wireOp",EDGE,"E6");Q12=makeQuery(id+"F8.boolean.opBoolean","SPLIT",EDGE,{"disambiguationData":[TD([makeQuery(id+"F8.opExtrude","SWEPT_FACE",FACE,{"disambiguationData":[OSD([sQuery(id+"F7.wireOp",EDGE,"E25.right")])]})])],"derivedFrom":makeQuery(id+"F2.opShell","OFFSET_EDGE",EDGE,{"disambiguationData":[OSD([subQ1,subQ0])]})});}
            var Q13;
            {var subQ0=sQuery(id+"F0.wireOp",EDGE,"E6");var subQ1=sQuery(id+"F0.wireOp",EDGE,"E7");Q13=makeQuery(id+"F8.boolean.opBoolean","SPLIT",EDGE,{"disambiguationData":[TD([makeQuery(id+"F8.opExtrude","SWEPT_FACE",FACE,{"disambiguationData":[OSD([sQuery(id+"F7.wireOp",EDGE,"E25.left")])]})])],"derivedFrom":makeQuery(id+"F2.opShell","OFFSET_EDGE",EDGE,{"disambiguationData":[OSD([subQ0,subQ1])]})});}
            var Q14;
            {var subQ0=sQuery(id+"F0.wireOp",EDGE,"E7");var subQ1=sQuery(id+"F0.wireOp",EDGE,"E6");Q14=makeQuery(id+"F8.boolean.opBoolean","SPLIT",EDGE,{"disambiguationData":[TD([makeQuery(id+"F8.opExtrude","SWEPT_FACE",FACE,{"disambiguationData":[OSD([sQuery(id+"F7.wireOp",EDGE,"E25.left")])]})])],"derivedFrom":makeQuery(id+"F1.opExtrude","SWEPT_EDGE",EDGE,{"disambiguationData":[OSD([subQ1,subQ0])]})});}
            var Q15;
            {var subQ0=sQuery(id+"F0.wireOp",EDGE,"E7");var subQ1=sQuery(id+"F0.wireOp",EDGE,"E6");Q15=makeQuery(id+"F8.boolean.opBoolean","SPLIT",EDGE,{"disambiguationData":[TD([makeQuery(id+"F8.opExtrude","SWEPT_FACE",FACE,{"disambiguationData":[OSD([sQuery(id+"F7.wireOp",EDGE,"E25.right")])]})])],"derivedFrom":makeQuery(id+"F1.opExtrude","SWEPT_EDGE",EDGE,{"disambiguationData":[OSD([subQ1,subQ0])]})});}
            var Q16;
            {var subQ0=sQuery(id+"F0.wireOp",EDGE,"E6");var subQ1=sQuery(id+"F0.wireOp",EDGE,"E5");Q16=makeQuery(id+"F8.boolean.opBoolean","SPLIT",EDGE,{"disambiguationData":[TD([makeQuery(id+"F8.opExtrude","SWEPT_FACE",FACE,{"disambiguationData":[OSD([sQuery(id+"F7.wireOp",EDGE,"E25.left")])]})])],"derivedFrom":makeQuery(id+"F1.opExtrude","SWEPT_EDGE",EDGE,{"disambiguationData":[OSD([subQ1,subQ0])]})});}
            var Q17;
            {var subQ0=sQuery(id+"F0.wireOp",EDGE,"E6");var subQ1=sQuery(id+"F0.wireOp",EDGE,"E5");Q17=makeQuery(id+"F8.boolean.opBoolean","SPLIT",EDGE,{"disambiguationData":[TD([makeQuery(id+"F8.opExtrude","SWEPT_FACE",FACE,{"disambiguationData":[OSD([sQuery(id+"F7.wireOp",EDGE,"E25.right")])]})])],"derivedFrom":makeQuery(id+"F1.opExtrude","SWEPT_EDGE",EDGE,{"disambiguationData":[OSD([subQ1,subQ0])]})});}
            var Q18;
            {var subQ0=sQuery(id+"F0.wireOp",EDGE,"E5");var subQ1=sQuery(id+"F0.wireOp",EDGE,"E6");Q18=makeQuery(id+"F8.boolean.opBoolean","SPLIT",EDGE,{"disambiguationData":[TD([makeQuery(id+"F8.opExtrude","SWEPT_FACE",FACE,{"disambiguationData":[OSD([sQuery(id+"F7.wireOp",EDGE,"E25.left")])]})])],"derivedFrom":makeQuery(id+"F2.opShell","OFFSET_EDGE",EDGE,{"disambiguationData":[OSD([subQ0,subQ1])]})});}
            var Q19;
            {var subQ0=sQuery(id+"F0.wireOp",EDGE,"E6");var subQ1=sQuery(id+"F0.wireOp",EDGE,"E5");Q19=makeQuery(id+"F8.boolean.opBoolean","SPLIT",EDGE,{"disambiguationData":[TD([makeQuery(id+"F8.opExtrude","SWEPT_FACE",FACE,{"disambiguationData":[OSD([sQuery(id+"F7.wireOp",EDGE,"E25.right")])]})])],"derivedFrom":makeQuery(id+"F2.opShell","OFFSET_EDGE",EDGE,{"disambiguationData":[OSD([subQ1,subQ0])]})});}
            var Q20;
            {var subQ0=sQuery(id+"F0.wireOp",EDGE,"E0.bottom");var subQ2=sQuery(id+"F0.wireOp",EDGE,"E0.left");Q20=makeQuery(id+"F8.boolean.opBoolean","SPLIT",EDGE,{"disambiguationData":[TD([makeQuery(id+"F8.opExtrude","SWEPT_FACE",FACE,{"disambiguationData":[OSD([sQuery(id+"F7.wireOp",EDGE,"E25.right")])]})])],"derivedFrom":makeQuery(id+"F2.opShell","OFFSET_EDGE",EDGE,{"disambiguationData":[OSD([subQ0,subQ2])]})});}
            var Q21;
            {var subQ0=sQuery(id+"F0.wireOp",EDGE,"E0.bottom");var subQ1=sQuery(id+"F0.wireOp",EDGE,"E0.left");Q21=makeQuery(id+"F8.boolean.opBoolean","SPLIT",EDGE,{"disambiguationData":[TD([makeQuery(id+"F8.opExtrude","SWEPT_FACE",FACE,{"disambiguationData":[OSD([sQuery(id+"F7.wireOp",EDGE,"E25.left")])]})])],"derivedFrom":makeQuery(id+"F2.opShell","OFFSET_EDGE",EDGE,{"disambiguationData":[OSD([subQ0,subQ1])]})});}
            var Q22;
            {var subQ0=sQuery(id+"F0.wireOp",EDGE,"E0.bottom");var subQ2=sQuery(id+"F0.wireOp",EDGE,"E0.left");Q22=makeQuery(id+"F8.boolean.opBoolean","SPLIT",EDGE,{"disambiguationData":[TD([makeQuery(id+"F8.opExtrude","SWEPT_FACE",FACE,{"disambiguationData":[OSD([sQuery(id+"F7.wireOp",EDGE,"E25.right")])]})])],"derivedFrom":makeQuery(id+"F1.opExtrude","SWEPT_EDGE",EDGE,{"disambiguationData":[OSD([subQ0,subQ2])]})});}
            var Q23;
            {var subQ0=sQuery(id+"F0.wireOp",EDGE,"E0.bottom");var subQ2=sQuery(id+"F0.wireOp",EDGE,"E0.left");Q23=makeQuery(id+"F8.boolean.opBoolean","SPLIT",EDGE,{"disambiguationData":[TD([makeQuery(id+"F8.opExtrude","SWEPT_FACE",FACE,{"disambiguationData":[OSD([sQuery(id+"F7.wireOp",EDGE,"E25.left")])]})])],"derivedFrom":makeQuery(id+"F1.opExtrude","SWEPT_EDGE",EDGE,{"disambiguationData":[OSD([subQ0,subQ2])]})});}
            fillet(context, id + "F20", {"entities" : qUnion([Q0, Q1, Q2, Q3, Q4, Q5, Q6, Q7, Q8, Q9, Q10, Q11, Q12, Q13, Q14, Q15, Q16, Q17, Q18, Q19, Q20, Q21, Q22, Q23]), "radius" : 20 * mm, "tangentPropagation" : true, "allowEdgeOverflow" : false});
        }
        {
            var Q0;
            Q0=makeQuery(id+"F19.opExtrude","CAP_FACE",FACE,{"disambiguationData":[OSD([sQuery(id+"F0.wireOp",EDGE,"E0.right"),sQuery(id+"F0.wireOp",EDGE,"E1"),sQuery(id+"F7.wireOp",EDGE,"E25.left")])],"isStart":false});
            var Q1;
            {var subQ0=sQuery(id+"F0.wireOp",EDGE,"E1");var subQ1=sQuery(id+"F0.wireOp",EDGE,"E0.right");var subQ2=makeQuery(id+"F2.opShell","OFFSET_FACE",FACE,{"disambiguationData":[OSD([subQ1,subQ0])]});var subQ26=sQuery(id+"F7.wireOp",EDGE,"E25.left");var subQ27=makeQuery(id+"F8.opExtrude","SWEPT_FACE",FACE,{"disambiguationData":[OSD([subQ26])]});var subQ29=makeQuery(id+"F12.opExtrude","SWEPT_FACE",FACE,{"disambiguationData":[OSD([sQuery(id+"F11.wireOp",EDGE,"E39")])]});var subQ30=subQ2;var subQ38=makeQuery(id+"F12.opExtrude","SWEPT_FACE",FACE,{"disambiguationData":[OSD([sQuery(id+"F11.wireOp",EDGE,"E38")])]});var subQ39=makeQuery(id+"F8.opExtrude","SWEPT_FACE",FACE,{"disambiguationData":[OSD([sQuery(id+"F7.wireOp",EDGE,"E25.right")])]});Q1=makeQuery(id+"F14.boolean.opBoolean","MERGE",FACE,{"derivedFrom":[makeQuery(id+"F12.boolean.opBoolean","SPLIT",FACE,{"disambiguationData":[TD([subQ38])],"derivedFrom":makeQuery(id+"F8.boolean.opBoolean","SPLIT",FACE,{"disambiguationData":[TD([subQ39])],"derivedFrom":subQ30})}),makeQuery(id+"F12.boolean.opBoolean","SPLIT",FACE,{"disambiguationData":[TD([subQ38])],"derivedFrom":makeQuery(id+"F8.boolean.opBoolean","SPLIT",FACE,{"disambiguationData":[TD([subQ27])],"derivedFrom":subQ30})}),makeQuery(id+"F14.opExtrude","SWEPT_FACE",FACE,{"disambiguationData":[OSD([subQ1,subQ0,subQ26]),TDD([makeQuery(id+"F8.boolean.opBoolean","INTERSECT",EDGE,{"disambiguationData":[OD(2.0)],"derivedFrom":[subQ30,subQ27]})])]}),makeQuery(id+"F14.opExtrude","SWEPT_FACE",FACE,{"disambiguationData":[OSD([subQ1,subQ0,subQ26]),TDD([makeQuery(id+"F12.boolean.opBoolean","SPLIT",EDGE,{"disambiguationData":[TD([subQ38])],"derivedFrom":makeQuery(id+"F8.boolean.opBoolean","INTERSECT",EDGE,{"disambiguationData":[OD(0.0)],"derivedFrom":[subQ30,subQ27]})})])]}),makeQuery(id+"F14.opExtrude","SWEPT_FACE",FACE,{"disambiguationData":[OSD([subQ1,subQ0,subQ26]),TDD([makeQuery(id+"F12.boolean.opBoolean","SPLIT",EDGE,{"disambiguationData":[TD([subQ29])],"derivedFrom":makeQuery(id+"F8.boolean.opBoolean","INTERSECT",EDGE,{"disambiguationData":[OD(1.0)],"derivedFrom":[subQ30,subQ27]})})])]})]});}
            var Q2;
            {var subQ0=sQuery(id+"F0.wireOp",EDGE,"E5");var subQ1=sQuery(id+"F0.wireOp",EDGE,"E0.left");var subQ2=makeQuery(id+"F2.opShell","OFFSET_FACE",FACE,{"disambiguationData":[OSD([subQ1,subQ0])]});var subQ26=sQuery(id+"F7.wireOp",EDGE,"E25.right");var subQ27=makeQuery(id+"F8.opExtrude","SWEPT_FACE",FACE,{"disambiguationData":[OSD([subQ26])]});var subQ29=makeQuery(id+"F10.opExtrude","SWEPT_FACE",FACE,{"disambiguationData":[OSD([sQuery(id+"F9.wireOp",EDGE,"E30")])]});var subQ30=subQ2;var subQ33=makeQuery(id+"F10.opExtrude","SWEPT_FACE",FACE,{"disambiguationData":[OSD([sQuery(id+"F9.wireOp",EDGE,"E29")])]});var subQ39=makeQuery(id+"F8.opExtrude","SWEPT_FACE",FACE,{"disambiguationData":[OSD([sQuery(id+"F7.wireOp",EDGE,"E25.left")])]});Q2=makeQuery(id+"F13.boolean.opBoolean","MERGE",FACE,{"derivedFrom":[makeQuery(id+"F10.boolean.opBoolean","SPLIT",FACE,{"disambiguationData":[TD([subQ33])],"derivedFrom":makeQuery(id+"F8.boolean.opBoolean","SPLIT",FACE,{"disambiguationData":[TD([subQ27])],"derivedFrom":subQ30})}),makeQuery(id+"F10.boolean.opBoolean","SPLIT",FACE,{"disambiguationData":[TD([subQ33])],"derivedFrom":makeQuery(id+"F8.boolean.opBoolean","SPLIT",FACE,{"disambiguationData":[TD([subQ39])],"derivedFrom":subQ30})}),makeQuery(id+"F13.opExtrude","SWEPT_FACE",FACE,{"disambiguationData":[OSD([subQ1,subQ0,subQ26]),TDD([makeQuery(id+"F8.boolean.opBoolean","INTERSECT",EDGE,{"disambiguationData":[OD(2.0)],"derivedFrom":[subQ30,subQ27]})])]}),makeQuery(id+"F13.opExtrude","SWEPT_FACE",FACE,{"disambiguationData":[OSD([subQ1,subQ0,subQ26]),TDD([makeQuery(id+"F10.boolean.opBoolean","SPLIT",EDGE,{"disambiguationData":[TD([subQ33])],"derivedFrom":makeQuery(id+"F8.boolean.opBoolean","INTERSECT",EDGE,{"disambiguationData":[OD(0.0)],"derivedFrom":[subQ30,subQ27]})})])]}),makeQuery(id+"F13.opExtrude","SWEPT_FACE",FACE,{"disambiguationData":[OSD([subQ1,subQ0,subQ26]),TDD([makeQuery(id+"F10.boolean.opBoolean","SPLIT",EDGE,{"disambiguationData":[TD([subQ29])],"derivedFrom":makeQuery(id+"F8.boolean.opBoolean","INTERSECT",EDGE,{"disambiguationData":[OD(1.0)],"derivedFrom":[subQ30,subQ27]})})])]})]});}
            var Q3;
            Q3=makeQuery(id+"F18.opExtrude","CAP_FACE",FACE,{"disambiguationData":[OSD([sQuery(id+"F0.wireOp",EDGE,"E0.left"),sQuery(id+"F0.wireOp",EDGE,"E5"),sQuery(id+"F7.wireOp",EDGE,"E25.right")])],"isStart":false});
            fillet(context, id + "F21", {"entities" : qUnion([Q0, Q1, Q2, Q3]), "radius" : 5 * mm, "tangentPropagation" : true, "allowEdgeOverflow" : false});
        }
    });
